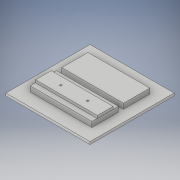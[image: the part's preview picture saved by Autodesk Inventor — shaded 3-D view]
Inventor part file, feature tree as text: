
AUTODESK INVENTOR PART (.ipt)
format: ipt  version: 2019.4 (Build 234330000, 330)  size: 147,968 bytes
history: native  units: in
note: dims shown in document units (in); Inventor stores cm internally (conversion verified against a paired STEP export)
features: extrude x4, sketch x4, projected_geometry x1
ambient origin geometry x8: Origin, YZ Plane, XZ Plane, XY Plane, X Axis, Y Axis, Z Axis, Center Point
bodies: Solid1 (feature_tree)
feature tree (9):
  extrude  "Extrusion1"  Depth=8.0in
  extrude  "Extrusion2"  Depth=0.25in TaperAngle=0.0deg
  extrude  "Extrusion3"  Depth=2.5in
  extrude  "Extrusion4"  Depth=1.25in
  sketch  "Sketch1"  dims[d0=8.0in d1=4.0in]
  sketch  "Sketch2"  dims[d2=4.0in d3=0.25in d4=0.0in]
  projected_geometry  "Projected Loop1"
  sketch  "Sketch3"  dims[d5=5.875in d6=2.5in]
  sketch  "Sketch4"  dims[d7=1.0625in d8=1.25in d9=2.5in d10=1.25in d11=0.5in d12=0.0in d13=1.5in d14=0.5in d15=0.25in d16=0.0in d17=0.1875in d18=0.75in d19=1.658in d21=0.1875in d22=1.658in d23=0.75in d24=0.0in]
